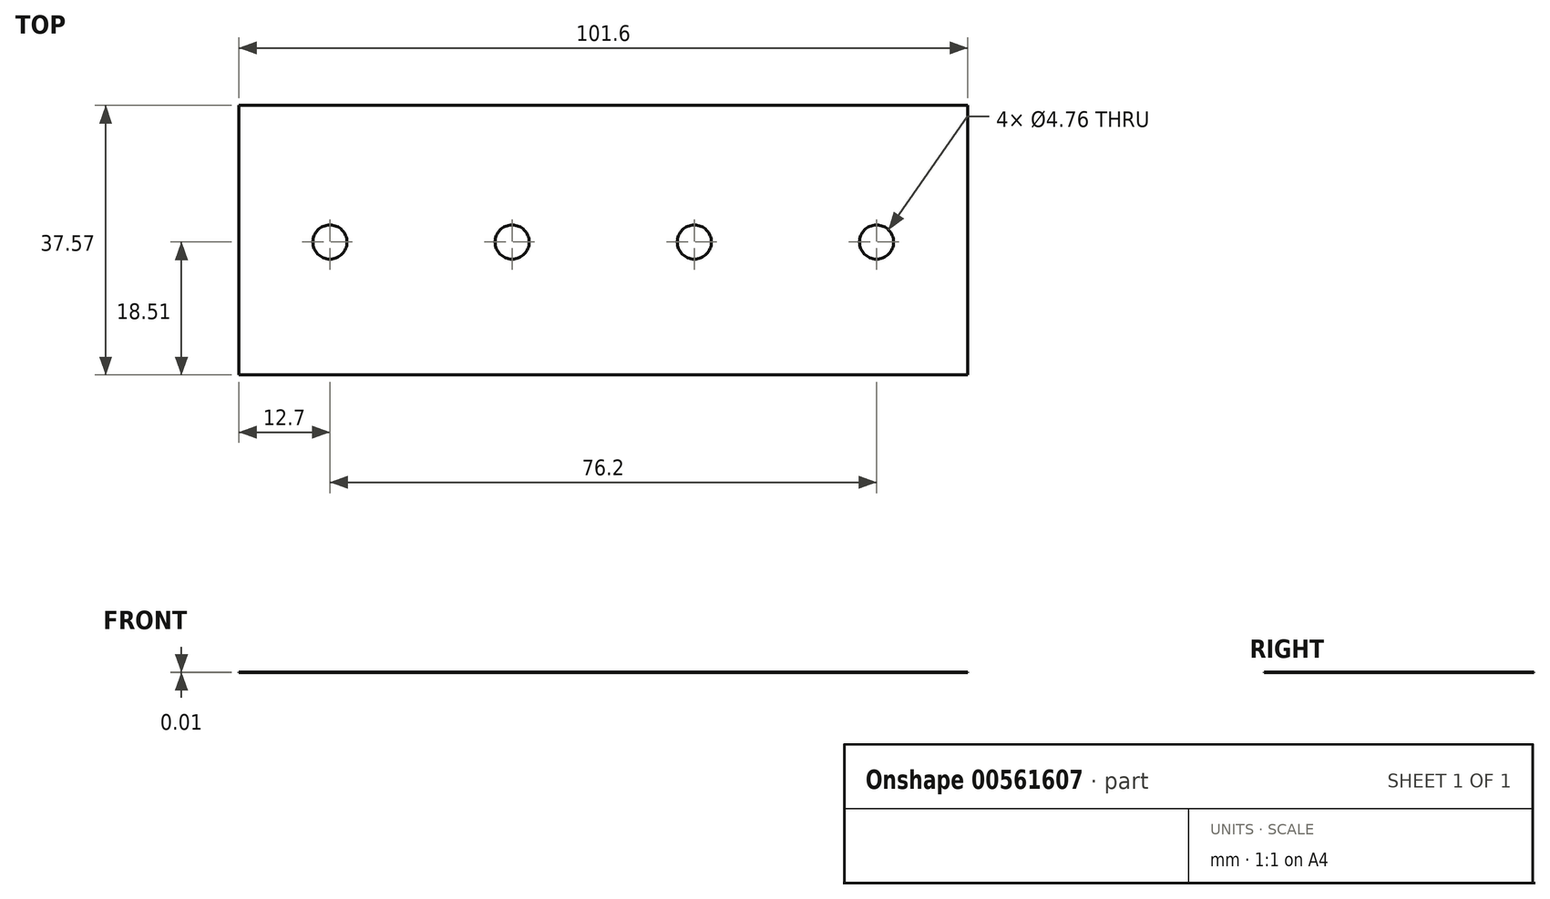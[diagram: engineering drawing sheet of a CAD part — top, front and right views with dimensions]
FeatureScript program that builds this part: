
annotation { "Feature Type Name" : "Feature", "Feature Type Description" : "" }
export const myFeature = defineFeature(function(context is Context, id is Id, definition is map)
    precondition{}
    {
        {
            assignVariable(context, id + "F0", {"name" : "plateHeight", "anyValue" : 1 / 101.6 * mm});
        }
        {
            var Q0;
            Q0=qCreatedBy(makeId("Top.planeOp"),FACE);
            var sketch = newSketch(context, id + "F1", { "sketchPlane" : qUnion([Q0])});
            skLineSegment(sketch, "E0.top", {"start": v(0, 25.4) * mm, "end": v(101.6, 25.4) * mm});
            skLineSegment(sketch, "E0.left", {"start": v(0, 0) * mm, "end": v(0, 25.4) * mm});
            skLineSegment(sketch, "E0.right", {"start": v(101.6, 0) * mm, "end": v(101.6, 25.4) * mm});
            skLineSegment(sketch, "E1", {"start": v(0, 0) * mm, "end": v(0, -12.16) * mm});
            skLineSegment(sketch, "E2", {"start": v(0, -12.16) * mm, "end": v(101.6, -12.16) * mm});
            skLineSegment(sketch, "E3", {"start": v(101.6, -12.16) * mm, "end": v(101.6, 0) * mm});
            skCircle(sketch, "E4", {"center": v(12.7, 6.35) * mm, "radius": 2.38 * mm});
            skCircle(sketch, "E5.1.0.0", {"center": v(38.1, 6.35) * mm, "radius": 2.38 * mm});
            skCircle(sketch, "E5.2.0.0", {"center": v(63.5, 6.35) * mm, "radius": 2.38 * mm});
            skLineSegment(sketch, "E5.direction1", {"start": v(12.7, 6.35) * mm, "end": v(38.1, 6.35) * mm, "construction": true});
            skCircle(sketch, "E6.0.3.0", {"center": v(88.9, 6.35) * mm, "radius": 2.38 * mm});
            skSolve(sketch);
        }
        {
            var Q0;
            Q0 = qSketchRegion(id + "F1", true);
            extrude(context, id + "F2", {"entities" : qUnion([Q0]), "depth" : getVariable(context, 'plateHeight'), "offsetDistance" : 25.4 * mm});
        }
    });
